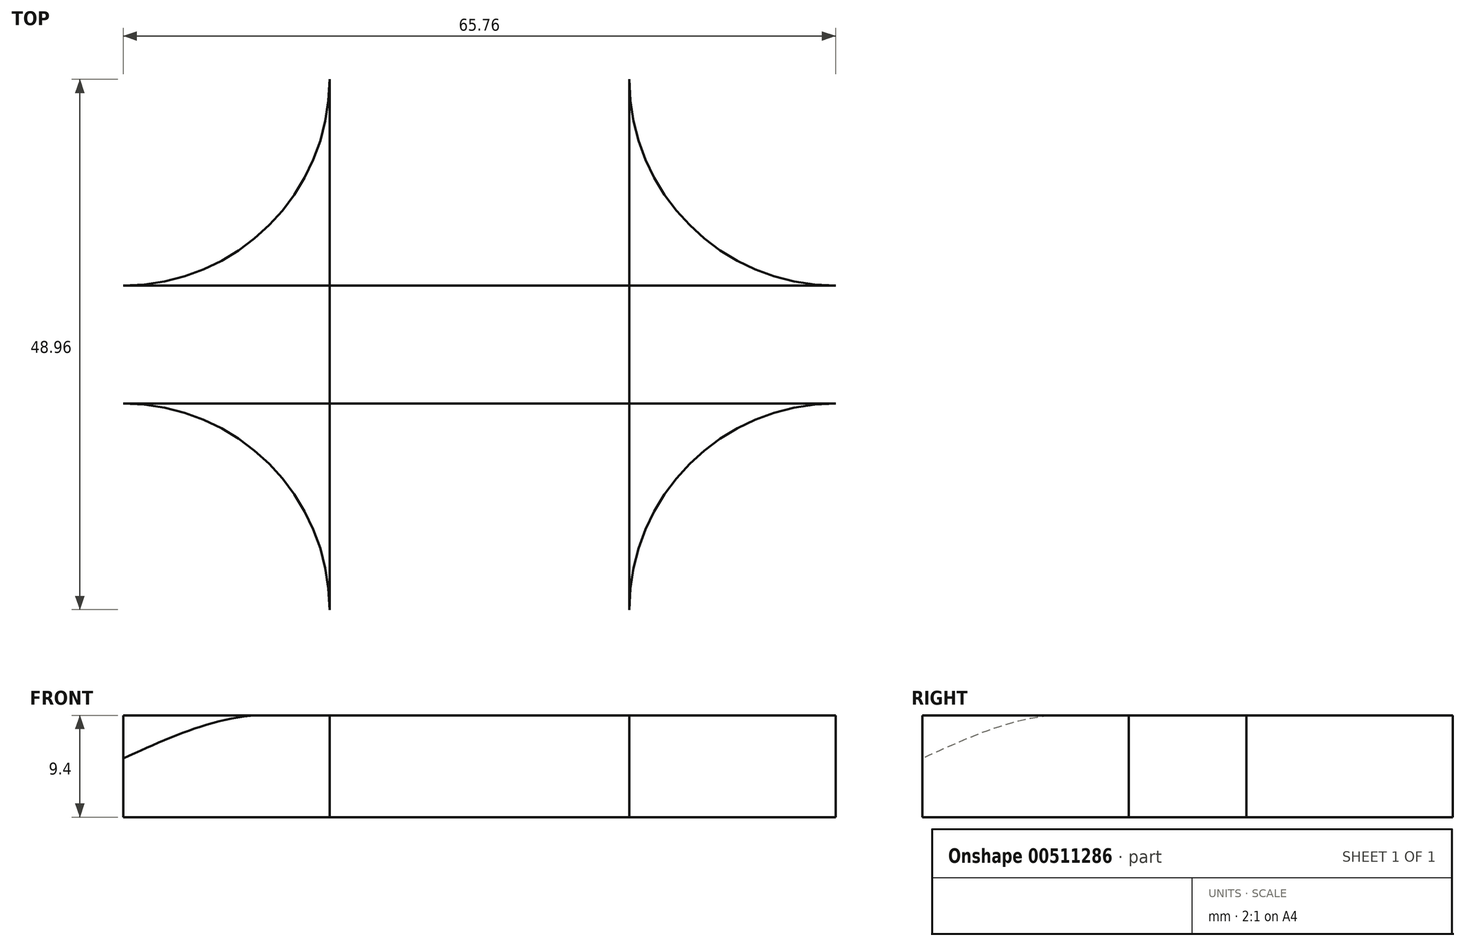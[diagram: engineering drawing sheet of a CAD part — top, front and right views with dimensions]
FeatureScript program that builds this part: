
annotation { "Feature Type Name" : "Feature", "Feature Type Description" : "" }
export const myFeature = defineFeature(function(context is Context, id is Id, definition is map)
    precondition{}
    {
        {
            var Q0;
            Q0=qCreatedBy(makeId("Top.planeOp"),FACE);
            var sketch = newSketch(context, id + "F0", { "sketchPlane" : qUnion([Q0])});
            skLineSegment(sketch, "E0.bottom", {"start": v(32.88, 30.83) * mm, "end": v(-32.88, 30.83) * mm});
            skLineSegment(sketch, "E0.top", {"start": v(32.88, -30.83) * mm, "end": v(-32.88, -30.83) * mm});
            skLineSegment(sketch, "E0.left", {"start": v(39.23, 24.48) * mm, "end": v(39.23, -24.48) * mm});
            skLineSegment(sketch, "E0.right", {"start": v(-39.23, 24.48) * mm, "end": v(-39.23, -24.48) * mm});
            skPoint(sketch, "E0.middle", {"position": v(0, 0) * mm});
            skPoint(sketch, "E1.visualSharp", {"position": v(-39.23, 30.83) * mm});
            skArc(sketch, "E1.filletArc", {"start": v(-32.88, 30.83) * mm, "mid": v(-37.37, 28.97) * mm, "end": v(-39.23, 24.48) * mm});
            skPoint(sketch, "E2.visualSharp", {"position": v(39.23, 30.83) * mm});
            skArc(sketch, "E2.filletArc", {"start": v(39.23, 24.48) * mm, "mid": v(37.37, 28.97) * mm, "end": v(32.88, 30.83) * mm});
            skPoint(sketch, "E3.visualSharp", {"position": v(39.23, -30.83) * mm});
            skArc(sketch, "E3.filletArc", {"start": v(32.88, -30.83) * mm, "mid": v(37.37, -28.97) * mm, "end": v(39.23, -24.48) * mm});
            skPoint(sketch, "E4.visualSharp", {"position": v(-39.23, -30.83) * mm});
            skArc(sketch, "E4.filletArc", {"start": v(-39.23, -24.48) * mm, "mid": v(-37.37, -28.97) * mm, "end": v(-32.88, -30.83) * mm});
            skArc(sketch, "E5.0", {"start": v(13.83, 24.48) * mm, "mid": v(19.41, 11.01) * mm, "end": v(32.88, 5.43) * mm});
            skLineSegment(sketch, "E5.1", {"start": v(13.83, 24.48) * mm, "end": v(13.83, -24.48) * mm});
            skLineSegment(sketch, "E5.2", {"start": v(32.88, 5.43) * mm, "end": v(-32.88, 5.43) * mm});
            skArc(sketch, "E5.3", {"start": v(32.88, -5.43) * mm, "mid": v(19.41, -11.01) * mm, "end": v(13.83, -24.48) * mm});
            skArc(sketch, "E5.4", {"start": v(-32.88, 5.43) * mm, "mid": v(-19.41, 11.01) * mm, "end": v(-13.83, 24.48) * mm});
            skLineSegment(sketch, "E5.5", {"start": v(-13.83, 24.48) * mm, "end": v(-13.83, -24.48) * mm});
            skArc(sketch, "E5.6", {"start": v(-13.83, -24.48) * mm, "mid": v(-19.41, -11.01) * mm, "end": v(-32.88, -5.43) * mm});
            skLineSegment(sketch, "E5.7", {"start": v(32.88, -5.43) * mm, "end": v(-32.88, -5.43) * mm});
            skSolve(sketch);
        }
        {
            var Q0;
            {var subQ0=sQuery(id+"F0.wireOp",EDGE,"E5.4");Q0=makeQuery(id+"F0.imprint","IMPRINT",FACE,{"disambiguationData":[TD([[makeQuery(id+"F0.imprint","IMPRINT",EDGE,{"derivedFrom":subQ0}),-1.0]])]});}
            var Q1;
            {var subQ0=sQuery(id+"F0.wireOp",EDGE,"E5.0");Q1=makeQuery(id+"F0.imprint","IMPRINT",FACE,{"disambiguationData":[TD([[makeQuery(id+"F0.imprint","IMPRINT",EDGE,{"derivedFrom":subQ0}),-1.0]])]});}
            var Q2;
            {var subQ0=sQuery(id+"F0.wireOp",EDGE,"E5.3");Q2=makeQuery(id+"F0.imprint","IMPRINT",FACE,{"disambiguationData":[TD([[makeQuery(id+"F0.imprint","IMPRINT",EDGE,{"derivedFrom":subQ0}),-1.0]])]});}
            var Q3;
            {var subQ0=sQuery(id+"F0.wireOp",EDGE,"E5.6");Q3=makeQuery(id+"F0.imprint","IMPRINT",FACE,{"disambiguationData":[TD([[makeQuery(id+"F0.imprint","IMPRINT",EDGE,{"derivedFrom":subQ0}),-1.0]])]});}
            var Q4;
            {var subQ0=sQuery(id+"F0.wireOp",EDGE,"E5.2");var subQ1=sQuery(id+"F0.wireOp",EDGE,"E5.1");var subQ2=makeQuery(id+"F0.imprint","INTERSECT",VERTEX,{"derivedFrom":[subQ1,subQ0]});Q4=makeQuery(id+"F0.imprint","IMPRINT",FACE,{"disambiguationData":[TD([[makeQuery(id+"F0.imprint","IMPRINT",EDGE,{"disambiguationData":[TD([[subQ2,-1.0]])],"derivedFrom":subQ1}),-1.0]])]});}
            extrude(context, id + "F1", {"entities" : qUnion([Q0, Q1, Q2, Q3, Q4]), "depth" : 9.4 * mm, "offsetDistance" : 25.4 * mm});
        }
        {
            var Q0;
            Q0=makeQuery(id+"F1.opExtrude","CAP_EDGE",EDGE,{"disambiguationData":[OSD([sQuery(id+"F0.wireOp",EDGE,"E5.6")])],"isStart":false});
            fillet(context, id + "F2", {"entities" : qUnion([Q0]), "tangentPropagation" : true, "radius" : 4 * mm, "defaultsChanged" : true, "vertexSettings" : [], "allowEdgeOverflow" : false});
        }
    });
